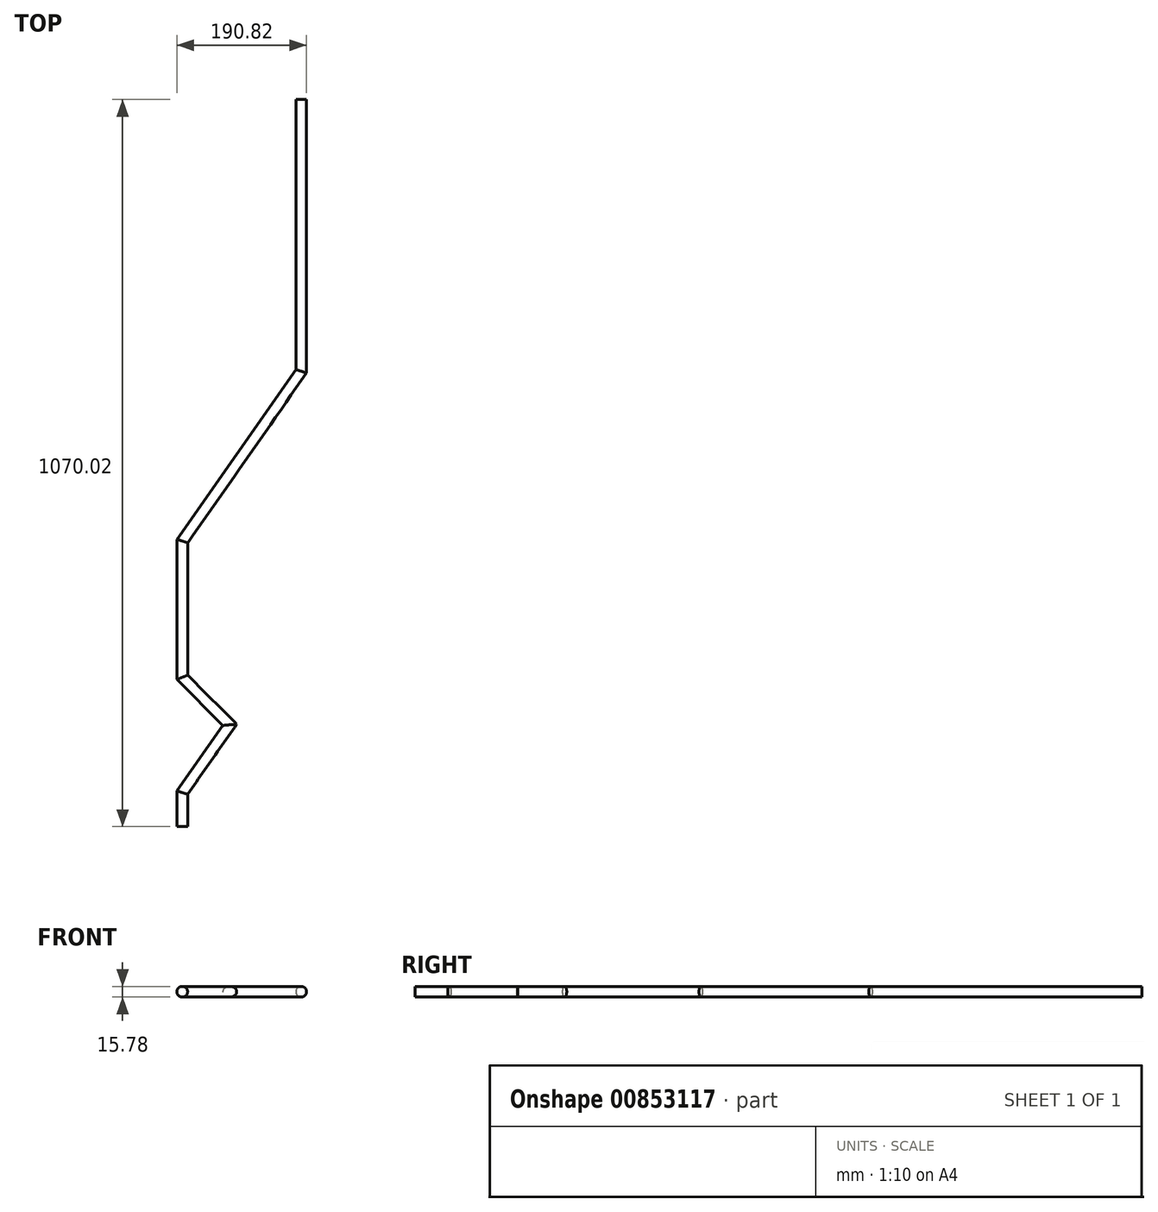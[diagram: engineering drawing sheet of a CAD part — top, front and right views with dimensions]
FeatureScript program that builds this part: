
annotation { "Feature Type Name" : "Feature", "Feature Type Description" : "" }
export const myFeature = defineFeature(function(context is Context, id is Id, definition is map)
    precondition{}
    {
        {
            var Q0;
            Q0=qCreatedBy(makeId("Top.planeOp"),FACE);
            var sketch = newSketch(context, id + "F0", { "sketchPlane" : qUnion([Q0])});
            skLineSegment(sketch, "E0", {"start": v(400, 0) * mm, "end": v(400, -400) * mm});
            skLineSegment(sketch, "E1", {"start": v(400, -400) * mm, "end": v(224.95, -650) * mm});
            skLineSegment(sketch, "E2", {"start": v(224.95, -650) * mm, "end": v(224.95, -850) * mm});
            skLineSegment(sketch, "E3", {"start": v(224.95, -850) * mm, "end": v(294.97, -920.02) * mm});
            skLineSegment(sketch, "E4", {"start": v(294.97, -920.02) * mm, "end": v(224.95, -1020.02) * mm});
            skLineSegment(sketch, "E5", {"start": v(224.95, -1020.02) * mm, "end": v(224.95, -1070.02) * mm});
            skSolve(sketch);
        }
        {
            var Q0;
            Q0=qCreatedBy(makeId("Front.planeOp"),FACE);
            var sketch = newSketch(context, id + "F1", { "sketchPlane" : qUnion([Q0])});
            skCircle(sketch, "E6", {"center": v(399.4, 0) * mm, "radius": 7.89 * mm});
            skSolve(sketch);
        }
        {
            var Q0;
            Q0 = qSketchRegion(id + "F1", true);
            var Q1;
            Q1 = qConstructionFilter(qBodyType(qCreatedBy(id + "F0" ,EDGE), BodyType.WIRE), ConstructionObject.NO);
            sweep(context, id + "F2", {"profiles" : qUnion([Q0]), "path" : qUnion([Q1])});
        }
    });
